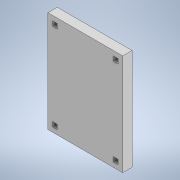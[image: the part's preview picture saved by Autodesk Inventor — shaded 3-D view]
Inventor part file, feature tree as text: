
AUTODESK INVENTOR PART (.ipt)
format: ipt  version: 2020.2 (Build 242310000, 310)  size: 186,880 bytes
history: native  units: mm
features: extrude x3, sketch x3
ambient origin geometry x8: Origin, YZ Plane, XZ Plane, XY Plane, X Axis, Y Axis, Z Axis, Center Point
bodies: Solide1 (feature_tree)
feature tree (6):
  extrude  "Extrusion1"  Depth=48.0mm
  extrude  "Extrusion2"  Depth=65.0mm
  extrude  "Extrusion4"  Depth=6.0mm TaperAngle=0.0deg
  sketch  "Esquisse1"
  sketch  "Esquisse2"
  sketch  "Esquisse4"
